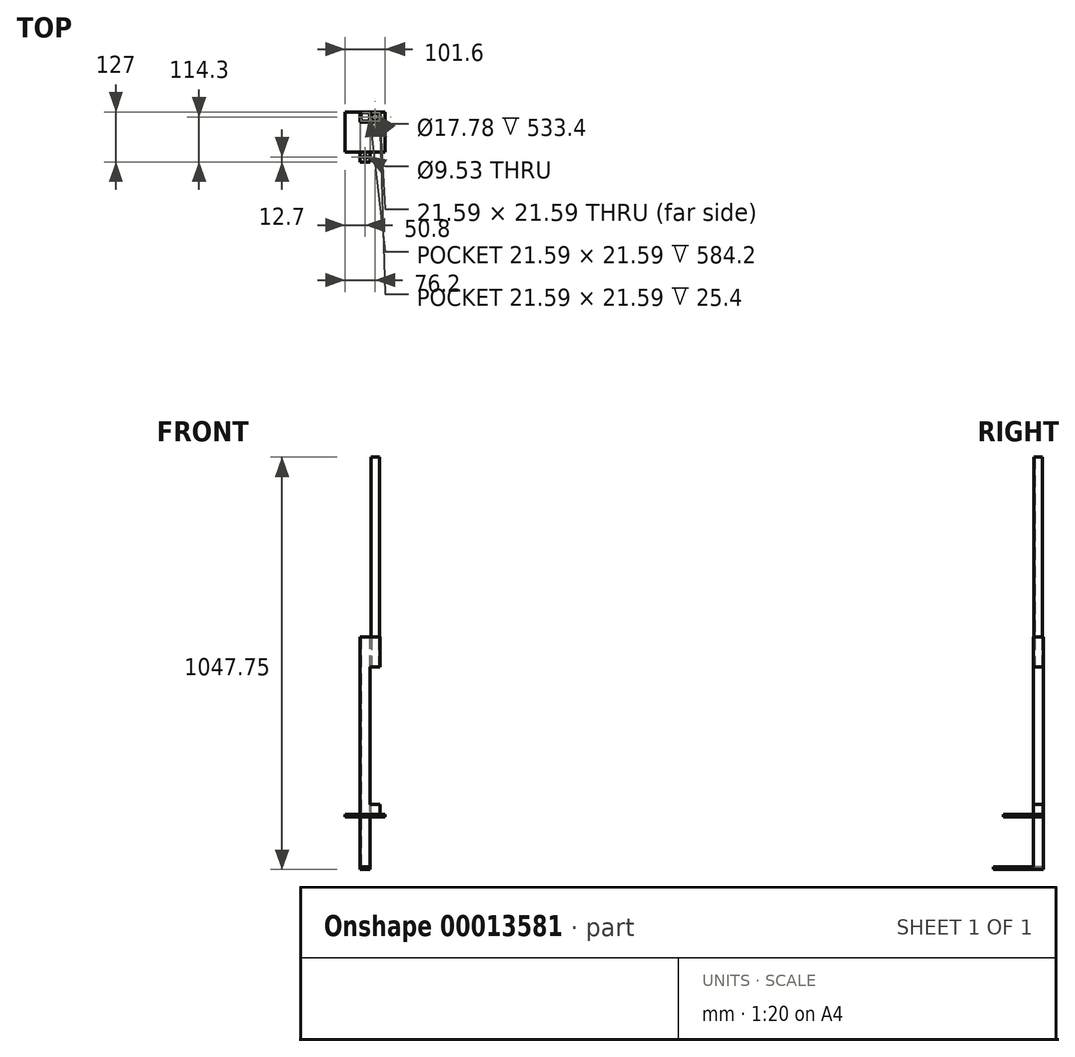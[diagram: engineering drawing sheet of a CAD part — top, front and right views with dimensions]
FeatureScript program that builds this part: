
annotation { "Feature Type Name" : "Feature", "Feature Type Description" : "" }
export const myFeature = defineFeature(function(context is Context, id is Id, definition is map)
    precondition{}
    {
        {
            var Q0;
            Q0=qCreatedBy(makeId("Top.planeOp"),FACE);
            var sketch = newSketch(context, id + "F0", { "sketchPlane" : qUnion([Q0])});
            skLineSegment(sketch, "E0.bottom", {"start": v(12.7, 12.7) * mm, "end": v(-12.7, 12.7) * mm});
            skLineSegment(sketch, "E0.top", {"start": v(12.7, -12.7) * mm, "end": v(-12.7, -12.7) * mm});
            skLineSegment(sketch, "E0.left", {"start": v(12.7, 12.7) * mm, "end": v(12.7, -12.7) * mm});
            skLineSegment(sketch, "E0.right", {"start": v(-12.7, 12.7) * mm, "end": v(-12.7, -12.7) * mm});
            skPoint(sketch, "E0.middle", {"position": v(0, 0) * mm});
            skLineSegment(sketch, "E1.bottom", {"start": v(10.8, 10.8) * mm, "end": v(-10.8, 10.8) * mm});
            skLineSegment(sketch, "E1.top", {"start": v(10.8, -10.8) * mm, "end": v(-10.8, -10.8) * mm});
            skLineSegment(sketch, "E1.left", {"start": v(10.8, 10.8) * mm, "end": v(10.8, -10.8) * mm});
            skLineSegment(sketch, "E1.right", {"start": v(-10.8, 10.8) * mm, "end": v(-10.8, -10.8) * mm});
            skSolve(sketch);
        }
        {
            var Q0;
            Q0 = qSketchRegion(id + "F0", true);
            extrude(context, id + "F1", {"entities" : qUnion([Q0]), "depth" : 457.2 * mm, "hasSecondDirection" : true, "secondDirectionOppositeDirection" : true, "secondDirectionDepth" : 127 * mm});
        }
        {
            var Q0;
            Q0=qCreatedBy(makeId("Top.planeOp"),FACE);
            var sketch = newSketch(context, id + "F2", { "sketchPlane" : qUnion([Q0])});
            skLineSegment(sketch, "E2.0", {"start": v(-12.7, 12.7) * mm, "end": v(-12.7, -12.7) * mm});
            skLineSegment(sketch, "E3.0", {"start": v(12.7, -12.7) * mm, "end": v(-12.7, -12.7) * mm});
            skLineSegment(sketch, "E4.0", {"start": v(12.7, 12.7) * mm, "end": v(12.7, -12.7) * mm});
            skLineSegment(sketch, "E5.bottom", {"start": v(-50.8, 12.7) * mm, "end": v(-12.7, 12.7) * mm});
            skLineSegment(sketch, "E5.top", {"start": v(-50.8, -88.9) * mm, "end": v(50.8, -88.9) * mm});
            skLineSegment(sketch, "E5.left", {"start": v(-50.8, 12.7) * mm, "end": v(-50.8, -88.9) * mm});
            skLineSegment(sketch, "E5.right", {"start": v(50.8, 12.7) * mm, "end": v(50.8, -88.9) * mm});
            skLineSegment(sketch, "E6.trimOffspring", {"start": v(12.7, 12.7) * mm, "end": v(50.8, 12.7) * mm});
            skSolve(sketch);
        }
        {
            var Q0;
            Q0 = qSketchRegion(id + "F2", true);
            extrude(context, id + "F3", {"entities" : qUnion([Q0]), "operationType" : NewBodyOperationType.ADD, "depth" : 6.35 * mm});
        }
        {
            var Q0;
            Q0=makeQuery(id+"F1.opExtrude","CAP_FACE",FACE,{"disambiguationData":[OSD([sQuery(id+"F0.wireOp",EDGE,"E0.bottom"),sQuery(id+"F0.wireOp",EDGE,"E0.top"),sQuery(id+"F0.wireOp",EDGE,"E0.left"),sQuery(id+"F0.wireOp",EDGE,"E0.right"),sQuery(id+"F0.wireOp",EDGE,"E1.bottom"),sQuery(id+"F0.wireOp",EDGE,"E1.top"),sQuery(id+"F0.wireOp",EDGE,"E1.left"),sQuery(id+"F0.wireOp",EDGE,"E1.right")])],"isStart":true});
            var sketch = newSketch(context, id + "F4", { "sketchPlane" : qUnion([Q0])});
            skLineSegment(sketch, "E7.bottom", {"start": v(-12.7, -12.7) * mm, "end": v(12.7, -12.7) * mm});
            skLineSegment(sketch, "E7.top", {"start": v(-12.7, 114.3) * mm, "end": v(12.7, 114.3) * mm});
            skLineSegment(sketch, "E7.left", {"start": v(-12.7, -12.7) * mm, "end": v(-12.7, 114.3) * mm});
            skLineSegment(sketch, "E7.right", {"start": v(12.7, -12.7) * mm, "end": v(12.7, 114.3) * mm});
            skCircle(sketch, "E8", {"center": v(0, 101.6) * mm, "radius": 4.76 * mm});
            skSolve(sketch);
        }
        {
            var Q0;
            Q0 = qSketchRegion(id + "F4", true);
            extrude(context, id + "F5", {"entities" : qUnion([Q0]), "operationType" : NewBodyOperationType.ADD, "depth" : 6.35 * mm});
        }
        {
            var Q0;
            Q0=makeQuery(id+"F1.opExtrude","CAP_FACE",FACE,{"disambiguationData":[OSD([sQuery(id+"F0.wireOp",EDGE,"E0.bottom"),sQuery(id+"F0.wireOp",EDGE,"E0.top"),sQuery(id+"F0.wireOp",EDGE,"E0.left"),sQuery(id+"F0.wireOp",EDGE,"E0.right"),sQuery(id+"F0.wireOp",EDGE,"E1.bottom"),sQuery(id+"F0.wireOp",EDGE,"E1.top"),sQuery(id+"F0.wireOp",EDGE,"E1.left"),sQuery(id+"F0.wireOp",EDGE,"E1.right")])],"isStart":false});
            var sketch = newSketch(context, id + "F6", { "sketchPlane" : qUnion([Q0])});
            skLineSegment(sketch, "E9.bottom", {"start": v(12.7, 12.7) * mm, "end": v(38.1, 12.7) * mm});
            skLineSegment(sketch, "E9.top", {"start": v(12.7, -12.7) * mm, "end": v(38.1, -12.7) * mm});
            skLineSegment(sketch, "E9.left", {"start": v(12.7, 12.7) * mm, "end": v(12.7, -12.7) * mm});
            skLineSegment(sketch, "E9.right", {"start": v(38.1, 12.7) * mm, "end": v(38.1, -12.7) * mm});
            skLineSegment(sketch, "E10", {"start": v(25.4, 12.7) * mm, "end": v(25.4, -12.7) * mm, "construction": true});
            skPoint(sketch, "E10.endSnap0", {"position": v(25.4, -12.7) * mm});
            skLineSegment(sketch, "E11.bottom", {"start": v(36.2, -10.8) * mm, "end": v(14.6, -10.8) * mm});
            skLineSegment(sketch, "E11.top", {"start": v(36.2, 10.8) * mm, "end": v(14.6, 10.8) * mm});
            skLineSegment(sketch, "E11.left", {"start": v(36.2, -10.8) * mm, "end": v(36.2, 10.8) * mm});
            skLineSegment(sketch, "E11.right", {"start": v(14.6, -10.8) * mm, "end": v(14.6, 10.8) * mm});
            skPoint(sketch, "E11.middle", {"position": v(25.4, 0) * mm});
            skSolve(sketch);
        }
        {
            var Q0;
            Q0=makeQuery(id+"F6.imprint","IMPRINT",FACE,{"disambiguationData":[TD([[makeQuery(id+"F6.imprint","IMPRINT",EDGE,{"derivedFrom":sQuery(id+"F6.wireOp",EDGE,"E9.bottom")}),-1.0]])]});
            var Q1;
            Q1=makeQuery(id+"F3.opExtrude","CAP_FACE",FACE,{"disambiguationData":[OSD([sQuery(id+"F2.wireOp",EDGE,"E2.0"),sQuery(id+"F2.wireOp",EDGE,"E3.0"),sQuery(id+"F2.wireOp",EDGE,"E4.0"),sQuery(id+"F2.wireOp",EDGE,"E5.bottom"),sQuery(id+"F2.wireOp",EDGE,"E5.top"),sQuery(id+"F2.wireOp",EDGE,"E5.left"),sQuery(id+"F2.wireOp",EDGE,"E5.right"),sQuery(id+"F2.wireOp",EDGE,"E6.trimOffspring")])],"isStart":false});
            extrude(context, id + "F7", {"entities" : qUnion([Q0]), "operationType" : NewBodyOperationType.ADD, "endBound" : BoundingType.UP_TO_SURFACE, "oppositeDirection" : true, "endBoundEntityFace" : qUnion([Q1]), "depth" : 25.4 * mm});
        }
        {
            var Q0;
            Q0=makeQuery(id+"F7.opExtrude","SWEPT_FACE",FACE,{"disambiguationData":[OSD([sQuery(id+"F6.wireOp",EDGE,"E9.right")])]});
            var sketch = newSketch(context, id + "F8", { "sketchPlane" : qUnion([Q0])});
            skLineSegment(sketch, "E12.bottom", {"start": v(-12.7, 457.2) * mm, "end": v(12.7, 457.2) * mm});
            skLineSegment(sketch, "E13.bottom", {"start": v(-12.7, 6.35) * mm, "end": v(12.7, 6.35) * mm});
            skLineSegment(sketch, "E13.top", {"start": v(-12.7, 31.75) * mm, "end": v(12.7, 31.75) * mm});
            skLineSegment(sketch, "E13.left", {"start": v(-12.7, 6.35) * mm, "end": v(-12.7, 31.75) * mm});
            skLineSegment(sketch, "E13.right", {"start": v(12.7, 6.35) * mm, "end": v(12.7, 31.75) * mm});
            skLineSegment(sketch, "E14.top", {"start": v(-12.7, 381) * mm, "end": v(12.7, 381) * mm});
            skLineSegment(sketch, "E14.left", {"start": v(-12.7, 457.2) * mm, "end": v(-12.7, 381) * mm});
            skLineSegment(sketch, "E14.right", {"start": v(12.7, 457.2) * mm, "end": v(12.7, 381) * mm});
            skLineSegment(sketch, "E15", {"start": v(-12.7, 381) * mm, "end": v(-12.7, 31.75) * mm});
            skLineSegment(sketch, "E16", {"start": v(12.7, 31.75) * mm, "end": v(12.7, 381) * mm});
            skSolve(sketch);
        }
        {
            var Q0;
            Q0=makeQuery(id+"F8.imprint","IMPRINT",FACE,{"disambiguationData":[TD([[makeQuery(id+"F8.imprint","IMPRINT",EDGE,{"derivedFrom":sQuery(id+"F8.wireOp",EDGE,"E13.top")}),1.0]])]});
            extrude(context, id + "F9", {"entities" : qUnion([Q0]), "operationType" : NewBodyOperationType.REMOVE, "oppositeDirection" : true, "depth" : 25.4 * mm});
        }
        {
            var Q0;
            Q0=makeQuery(id+"F9.boolean.opBoolean","COPY",FACE,{"derivedFrom":makeQuery(id+"F9.opExtrude","SWEPT_FACE",FACE,{"disambiguationData":[OSD([sQuery(id+"F8.wireOp",EDGE,"E14.top")])]})});
            var sketch = newSketch(context, id + "F10", { "sketchPlane" : qUnion([Q0])});
            skCircle(sketch, "E17", {"center": v(25.4, 0) * mm, "radius": 10.8 * mm});
            skCircle(sketch, "E18", {"center": v(25.4, 0) * mm, "radius": 8.9 * mm});
            skSolve(sketch);
        }
        {
            var Q0;
            Q0 = qSketchRegion(id + "F10", true);
            extrude(context, id + "F11", {"entities" : qUnion([Q0]), "oppositeDirection" : true, "depth" : 533.4 * mm});
        }
    });
